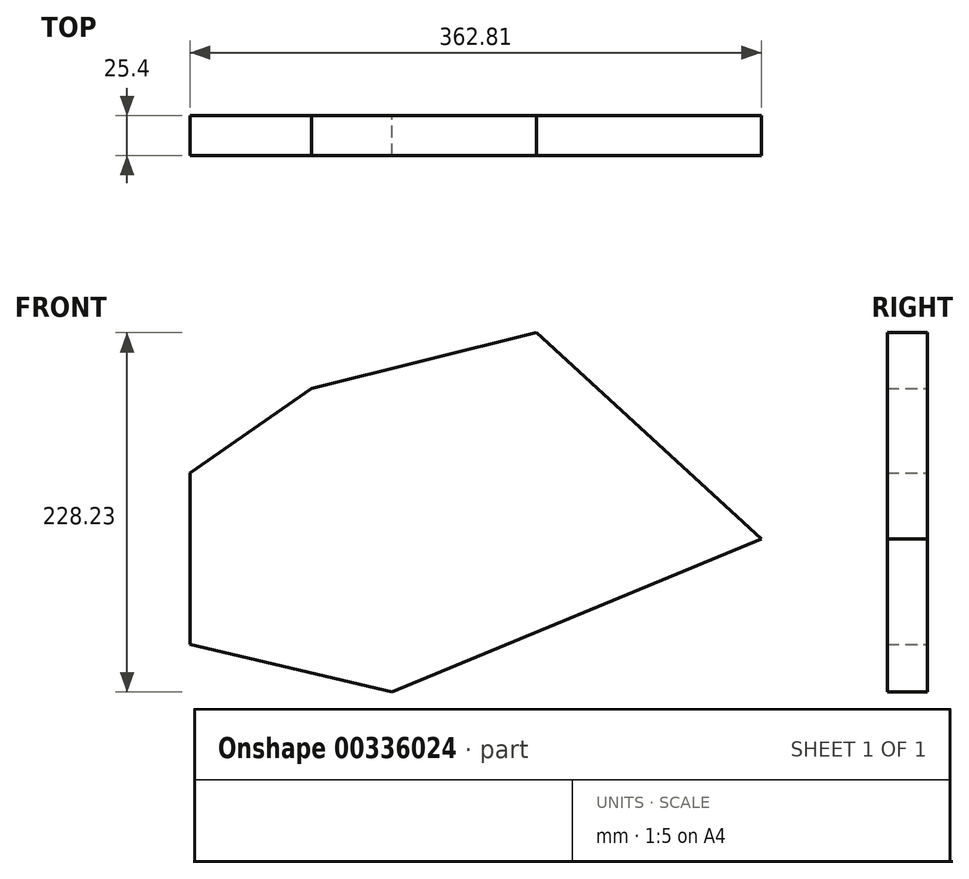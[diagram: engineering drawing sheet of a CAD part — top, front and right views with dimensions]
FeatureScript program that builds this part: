
annotation { "Feature Type Name" : "Feature", "Feature Type Description" : "" }
export const myFeature = defineFeature(function(context is Context, id is Id, definition is map)
    precondition{}
    {
        {
            var Q0;
            Q0=qCreatedBy(makeId("Front.planeOp"),FACE);
            var sketch = newSketch(context, id + "F0", { "sketchPlane" : qUnion([Q0])});
            skLineSegment(sketch, "E0", {"start": v(-75.64, 75.8) * mm, "end": v(-152.6, 22.1) * mm});
            skLineSegment(sketch, "E1", {"start": v(-152.6, 22.1) * mm, "end": v(-152.6, -86.94) * mm});
            skLineSegment(sketch, "E2", {"start": v(-152.6, -86.94) * mm, "end": v(-24.23, -117.06) * mm});
            skLineSegment(sketch, "E3", {"start": v(-24.23, -117.06) * mm, "end": v(210.22, -19.81) * mm});
            skLineSegment(sketch, "E4", {"start": v(210.22, -19.81) * mm, "end": v(67.45, 111.17) * mm});
            skLineSegment(sketch, "E5", {"start": v(67.45, 111.17) * mm, "end": v(-75.64, 75.8) * mm});
            skSolve(sketch);
        }
        {
            var Q0;
            Q0=makeQuery(id+"F0.imprint","IMPRINT",FACE,{"disambiguationData":[TD([[makeQuery(id+"F0.imprint","IMPRINT",EDGE,{"derivedFrom":sQuery(id+"F0.wireOp",EDGE,"E0")}),1.0]])]});
            extrude(context, id + "F1", {"entities" : qUnion([Q0]), "depth" : 25.4 * mm});
        }
    });
